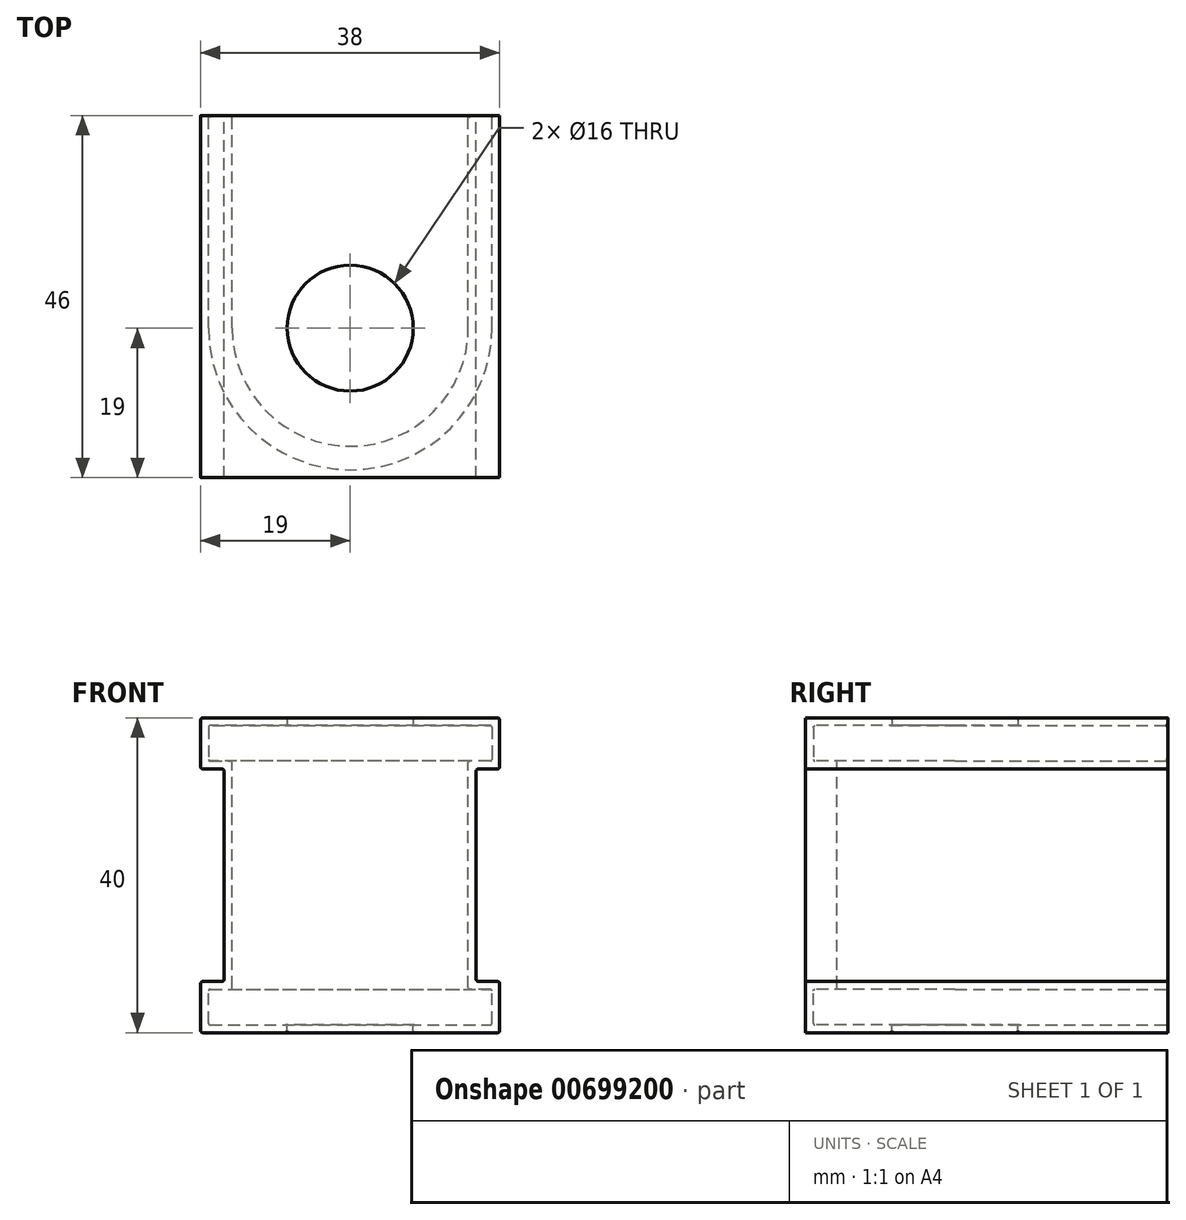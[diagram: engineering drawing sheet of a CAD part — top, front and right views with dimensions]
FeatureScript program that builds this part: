
annotation { "Feature Type Name" : "Feature", "Feature Type Description" : "" }
export const myFeature = defineFeature(function(context is Context, id is Id, definition is map)
    precondition{}
    {
        {
            var Q0;
            Q0=qCreatedBy(makeId("Top.planeOp"),FACE);
            var sketch = newSketch(context, id + "F0", { "sketchPlane" : qUnion([Q0])});
            skCircle(sketch, "E0", {"center": v(0, 0) * mm, "radius": 8 * mm});
            skArc(sketch, "E1", {"start": v(-15, 0) * mm, "mid": v(0, -15) * mm, "end": v(15, 0) * mm});
            skArc(sketch, "E2", {"start": v(-18, 0) * mm, "mid": v(0, -18) * mm, "end": v(18, 0) * mm});
            skLineSegment(sketch, "E3", {"start": v(-18, 0) * mm, "end": v(-18, 17) * mm});
            skLineSegment(sketch, "E4", {"start": v(-18, 17) * mm, "end": v(0, 17) * mm});
            skLineSegment(sketch, "E5", {"start": v(18, 0) * mm, "end": v(18, 17) * mm});
            skLineSegment(sketch, "E6", {"start": v(18, 17) * mm, "end": v(0, 17) * mm});
            skLineSegment(sketch, "E7", {"start": v(-15, 0) * mm, "end": v(-15, 17) * mm});
            skLineSegment(sketch, "E8", {"start": v(15, 0) * mm, "end": v(15, 17) * mm});
            skLineSegment(sketch, "E9.0", {"start": v(-19, 18) * mm, "end": v(0, 18) * mm});
            skLineSegment(sketch, "E9.1", {"start": v(-19, 0) * mm, "end": v(-19, 18) * mm});
            skLineSegment(sketch, "E9.2", {"start": v(19, 18) * mm, "end": v(0, 18) * mm});
            skLineSegment(sketch, "E9.3", {"start": v(19, 0) * mm, "end": v(19, 18) * mm});
            skArc(sketch, "E9.4", {"start": v(-19, 0) * mm, "mid": v(0, -19) * mm, "end": v(19, 0) * mm});
            skLineSegment(sketch, "E10", {"start": v(-19, 0) * mm, "end": v(-19, -19) * mm});
            skPoint(sketch, "E10.endSnap0", {"position": v(0, -19) * mm});
            skLineSegment(sketch, "E11", {"start": v(-19, -19) * mm, "end": v(0, -19) * mm});
            skLineSegment(sketch, "E12", {"start": v(19, 0) * mm, "end": v(19, -19) * mm});
            skLineSegment(sketch, "E13", {"start": v(19, -19) * mm, "end": v(0, -19) * mm});
            skSolve(sketch);
        }
        {
            var Q0;
            Q0=makeQuery(id+"F0.imprint","IMPRINT",FACE,{"disambiguationData":[TD([[makeQuery(id+"F0.imprint","IMPRINT",EDGE,{"derivedFrom":sQuery(id+"F0.wireOp",EDGE,"E2")}),-1.0]])]});
            extrude(context, id + "F1", {"entities" : qUnion([Q0]), "oppositeDirection" : true, "depth" : (38 / 2 + 1) * mm, "offsetDistance" : 25 * mm});
        }
        {
            var Q0;
            Q0=makeQuery(id+"F0.imprint","IMPRINT",FACE,{"disambiguationData":[TD([[makeQuery(id+"F0.imprint","IMPRINT",EDGE,{"derivedFrom":sQuery(id+"F0.wireOp",EDGE,"E0")}),-1.0]])]});
            extrude(context, id + "F2", {"entities" : qUnion([Q0]), "operationType" : NewBodyOperationType.ADD, "oppositeDirection" : true, "depth" : (38 / 2 + 1) * mm, "offsetDistance" : 25 * mm, "hasSecondDirection" : true, "secondDirectionOppositeDirection" : true, "secondDirectionDepth" : (38 / 2) * mm});
        }
        {
            var Q0;
            {var subQ0=makeQuery(id+"F1.opExtrude","SWEPT_FACE",FACE,{"disambiguationData":[OSD([sQuery(id+"F0.wireOp",EDGE,"E9.0"),sQuery(id+"F0.wireOp",EDGE,"E9.2")])]});Q0=makeQuery(id+"FkgVPa9aZE5Qvnv_1.boolean.opBoolean","MERGE",FACE,{"derivedFrom":[subQ0,makeQuery(id+"FkgVPa9aZE5Qvnv_1.opPattern","COPY",FACE,{"derivedFrom":subQ0,"instanceName":"1"})]});}
            extrude(context, id + "F3", {"entities" : qUnion([Q0]), "operationType" : NewBodyOperationType.REMOVE, "oppositeDirection" : true, "depth" : 1 * mm, "offsetDistance" : 25 * mm});
        }
        {
            var Q0;
            Q0=makeQuery(id+"F0.imprint","IMPRINT",FACE,{"disambiguationData":[TD([[makeQuery(id+"F0.imprint","IMPRINT",EDGE,{"derivedFrom":sQuery(id+"F0.wireOp",EDGE,"E1")}),-1.0]])]});
            extrude(context, id + "F4", {"entities" : qUnion([Q0]), "operationType" : NewBodyOperationType.ADD, "oppositeDirection" : true, "depth" : 20 * mm, "offsetDistance" : 25 * mm, "hasSecondDirection" : true, "secondDirectionOppositeDirection" : true, "secondDirectionDepth" : 19 * mm});
        }
        {
            var Q0;
            Q0=makeQuery(id+"F0.imprint","IMPRINT",FACE,{"disambiguationData":[TD([[makeQuery(id+"F0.imprint","IMPRINT",EDGE,{"derivedFrom":sQuery(id+"F0.wireOp",EDGE,"E1")}),-1.0]])]});
            extrude(context, id + "F5", {"entities" : qUnion([Q0]), "operationType" : NewBodyOperationType.ADD, "oppositeDirection" : true, "depth" : (29 / 2) * mm, "offsetDistance" : 25 * mm});
        }
        {
            var Q0;
            {var subQ0=sQuery(id+"F0.wireOp",EDGE,"E10");Q0=makeQuery(id+"F0.imprint","IMPRINT",FACE,{"disambiguationData":[TD([[makeQuery(id+"F0.imprint","IMPRINT",EDGE,{"derivedFrom":subQ0}),1.0]])]});}
            var Q1;
            {var subQ0=sQuery(id+"F0.wireOp",EDGE,"E12");Q1=makeQuery(id+"F0.imprint","IMPRINT",FACE,{"disambiguationData":[TD([[makeQuery(id+"F0.imprint","IMPRINT",EDGE,{"derivedFrom":subQ0}),-1.0]])]});}
            extrude(context, id + "F6", {"entities" : qUnion([Q0, Q1]), "operationType" : NewBodyOperationType.ADD, "oppositeDirection" : true, "depth" : 20 * mm, "offsetDistance" : 25 * mm});
        }
        {
            var Q0;
            Q0=makeQuery(id+"F3.boolean.opBoolean","SPLIT",BODY,{"disambiguationData":[OD(0.0)],"derivedFrom":makeQuery(id+"F1.opExtrude","SWEPT_BODY",BODY,{"disambiguationData":[OSD([sQuery(id+"F0.wireOp",EDGE,"E2"),sQuery(id+"F0.wireOp",EDGE,"E3"),sQuery(id+"F0.wireOp",EDGE,"E4"),sQuery(id+"F0.wireOp",EDGE,"E5"),sQuery(id+"F0.wireOp",EDGE,"E6"),sQuery(id+"F0.wireOp",EDGE,"E9.0"),sQuery(id+"F0.wireOp",EDGE,"E9.1"),sQuery(id+"F0.wireOp",EDGE,"E9.2"),sQuery(id+"F0.wireOp",EDGE,"E9.3"),sQuery(id+"F0.wireOp",EDGE,"E9.4")])]})});
            var Q1;
            Q1=qCreatedBy(makeId("Top.planeOp"),FACE);
            mirror(context, id + "F7", {"operationType" : NewBodyOperationType.ADD, "entities" : qUnion([Q0]), "mirrorPlane" : qUnion([Q1])});
        }
        {
            var Q0;
            {var subQ0=sQuery(id+"F0.wireOp",EDGE,"E6");var subQ1=sQuery(id+"F0.wireOp",EDGE,"E4");var subQ3=sQuery(id+"F0.wireOp",EDGE,"E5");var subQ5=sQuery(id+"F0.wireOp",EDGE,"E9.2");var subQ7=sQuery(id+"F0.wireOp",EDGE,"E9.0");var subQ8=sQuery(id+"F0.wireOp",EDGE,"E3");var subQ13=sQuery(id+"F0.wireOp",EDGE,"E7");var subQ17=makeQuery(id+"F3.opExtrude","CAP_FACE",FACE,{"disambiguationData":[OSD([subQ7,subQ5])],"isStart":false});var subQ18=makeQuery(id+"F5.boolean.opBoolean","MERGE",FACE,{"derivedFrom":[makeQuery(id+"F4.boolean.opBoolean","MERGE",FACE,{"derivedFrom":[makeQuery(id+"F3.boolean.opBoolean","COPY",FACE,{"disambiguationData":[TD([makeQuery(id+"F2.opExtrude","SWEPT_FACE",FACE,{"disambiguationData":[OSD([subQ13])]})])],"derivedFrom":subQ17}),makeQuery(id+"F3.boolean.opBoolean","COPY",FACE,{"disambiguationData":[TD([makeQuery(id+"F1.opExtrude","SWEPT_FACE",FACE,{"disambiguationData":[OSD([subQ8])]})])],"derivedFrom":subQ17}),makeQuery(id+"F3.boolean.opBoolean","COPY",FACE,{"disambiguationData":[TD([makeQuery(id+"F1.opExtrude","SWEPT_FACE",FACE,{"disambiguationData":[OSD([subQ3])]})])],"derivedFrom":subQ17}),makeQuery(id+"F4.opExtrude","SWEPT_FACE",FACE,{"disambiguationData":[OSD([subQ1])]}),makeQuery(id+"F4.opExtrude","SWEPT_FACE",FACE,{"disambiguationData":[OSD([subQ0])]})]}),makeQuery(id+"F5.opExtrude","SWEPT_FACE",FACE,{"disambiguationData":[OSD([subQ1])]}),makeQuery(id+"F5.opExtrude","SWEPT_FACE",FACE,{"disambiguationData":[OSD([subQ0])]})]});Q0=makeQuery(id+"F7.boolean.opBoolean","MERGE",FACE,{"derivedFrom":[subQ18,makeQuery(id+"F7.opPattern","COPY",FACE,{"derivedFrom":subQ18,"instanceName":"1"})]});}
            var sketch = newSketch(context, id + "F8", { "sketchPlane" : qUnion([Q0])});
            skLineSegment(sketch, "E14", {"start": v(-19, 13.5) * mm, "end": v(-16, 13.5) * mm});
            skLineSegment(sketch, "E15", {"start": v(-16, 13.5) * mm, "end": v(-16, -13.5) * mm});
            skLineSegment(sketch, "E16", {"start": v(-16, -13.5) * mm, "end": v(-19, -13.5) * mm});
            skLineSegment(sketch, "E17", {"start": v(-19, -13.5) * mm, "end": v(-19, 13.5) * mm});
            skLineSegment(sketch, "E18.MirrorCS", {"start": v(-13, 13.5) * mm, "end": v(-16, 13.5) * mm});
            skLineSegment(sketch, "E19.MirrorCS", {"start": v(16, 13.5) * mm, "end": v(16, -13.5) * mm});
            skLineSegment(sketch, "E20.MirrorCS", {"start": v(19, 13.5) * mm, "end": v(16, 13.5) * mm});
            skLineSegment(sketch, "E21.MirrorCS", {"start": v(19, -13.5) * mm, "end": v(19, 13.5) * mm});
            skLineSegment(sketch, "E22.MirrorCS", {"start": v(16, -13.5) * mm, "end": v(19, -13.5) * mm});
            skSolve(sketch);
        }
        {
            var Q0;
            Q0 = qSketchRegion(id + "F8", true);
            extrude(context, id + "F9", {"entities" : qUnion([Q0]), "operationType" : NewBodyOperationType.REMOVE, "oppositeDirection" : true, "depth" : 38.8 * mm, "offsetDistance" : 25 * mm});
        }
        {
            var Q0;
            {var subQ0=sQuery(id+"F0.wireOp",EDGE,"E6");var subQ1=sQuery(id+"F0.wireOp",EDGE,"E4");var subQ3=sQuery(id+"F0.wireOp",EDGE,"E5");var subQ5=sQuery(id+"F0.wireOp",EDGE,"E9.2");var subQ7=sQuery(id+"F0.wireOp",EDGE,"E9.0");var subQ8=sQuery(id+"F0.wireOp",EDGE,"E3");var subQ13=sQuery(id+"F0.wireOp",EDGE,"E7");var subQ17=makeQuery(id+"F3.opExtrude","CAP_FACE",FACE,{"disambiguationData":[OSD([subQ7,subQ5])],"isStart":false});var subQ18=makeQuery(id+"F5.boolean.opBoolean","MERGE",FACE,{"derivedFrom":[makeQuery(id+"F4.boolean.opBoolean","MERGE",FACE,{"derivedFrom":[makeQuery(id+"F3.boolean.opBoolean","COPY",FACE,{"disambiguationData":[TD([makeQuery(id+"F2.opExtrude","SWEPT_FACE",FACE,{"disambiguationData":[OSD([subQ13])]})])],"derivedFrom":subQ17}),makeQuery(id+"F3.boolean.opBoolean","COPY",FACE,{"disambiguationData":[TD([makeQuery(id+"F1.opExtrude","SWEPT_FACE",FACE,{"disambiguationData":[OSD([subQ8])]})])],"derivedFrom":subQ17}),makeQuery(id+"F3.boolean.opBoolean","COPY",FACE,{"disambiguationData":[TD([makeQuery(id+"F1.opExtrude","SWEPT_FACE",FACE,{"disambiguationData":[OSD([subQ3])]})])],"derivedFrom":subQ17}),makeQuery(id+"F4.opExtrude","SWEPT_FACE",FACE,{"disambiguationData":[OSD([subQ1])]}),makeQuery(id+"F4.opExtrude","SWEPT_FACE",FACE,{"disambiguationData":[OSD([subQ0])]})]}),makeQuery(id+"F5.opExtrude","SWEPT_FACE",FACE,{"disambiguationData":[OSD([subQ1])]}),makeQuery(id+"F5.opExtrude","SWEPT_FACE",FACE,{"disambiguationData":[OSD([subQ0])]})]});Q0=makeQuery(id+"F7.boolean.opBoolean","MERGE",FACE,{"derivedFrom":[subQ18,makeQuery(id+"F7.opPattern","COPY",FACE,{"derivedFrom":subQ18,"instanceName":"1"})]});}
            extrude(context, id + "F10", {"entities" : qUnion([Q0]), "operationType" : NewBodyOperationType.ADD, "depth" : 10 * mm, "offsetDistance" : 25 * mm});
        }
        {
            var Q0;
            {var subQ0=sQuery(id+"F0.wireOp",EDGE,"E7");var subQ1=sQuery(id+"F0.wireOp",EDGE,"E4");Q0=makeQuery(id+"F10.boolean.opBoolean","MERGE",EDGE,{"derivedFrom":[makeQuery(id+"F7.opPattern","COPY",EDGE,{"derivedFrom":makeQuery(id+"F5.opExtrude","CAP_EDGE",EDGE,{"disambiguationData":[OSD([subQ0])],"isStart":false}),"instanceName":"1"}),makeQuery(id+"F10.opExtrude","SWEPT_EDGE",EDGE,{"disambiguationData":[OSD([subQ1,subQ0]),TDD([makeQuery(id+"F7.opPattern","COPY",VERTEX,{"derivedFrom":makeQuery(id+"F5.opExtrude","CAP_VERTEX",VERTEX,{"disambiguationData":[OSD([subQ1,subQ0])],"isStart":false}),"instanceName":"1"})])]})]});}
            var Q1;
            Q1=makeQuery(id+"F7.opPattern","COPY",EDGE,{"derivedFrom":makeQuery(id+"F5.opExtrude","CAP_EDGE",EDGE,{"disambiguationData":[OSD([sQuery(id+"F0.wireOp",EDGE,"E1")])],"isStart":false}),"instanceName":"1"});
            var Q2;
            {var subQ0=sQuery(id+"F0.wireOp",EDGE,"E7");var subQ1=sQuery(id+"F0.wireOp",EDGE,"E4");Q2=makeQuery(id+"F10.boolean.opBoolean","MERGE",EDGE,{"derivedFrom":[makeQuery(id+"F5.opExtrude","CAP_EDGE",EDGE,{"disambiguationData":[OSD([subQ0])],"isStart":false}),makeQuery(id+"F10.opExtrude","SWEPT_EDGE",EDGE,{"disambiguationData":[OSD([subQ1,subQ0]),TDD([makeQuery(id+"F5.opExtrude","CAP_VERTEX",VERTEX,{"disambiguationData":[OSD([subQ1,subQ0])],"isStart":false})])]})]});}
            var Q3;
            Q3=makeQuery(id+"F5.opExtrude","CAP_EDGE",EDGE,{"disambiguationData":[OSD([sQuery(id+"F0.wireOp",EDGE,"E1")])],"isStart":false});
            var Q4;
            {var subQ0=sQuery(id+"F0.wireOp",EDGE,"E4");var subQ1=sQuery(id+"F0.wireOp",EDGE,"E3");Q4=makeQuery(id+"F10.boolean.opBoolean","MERGE",EDGE,{"derivedFrom":[makeQuery(id+"F7.opPattern","COPY",EDGE,{"derivedFrom":makeQuery(id+"F5.opExtrude","CAP_EDGE",EDGE,{"disambiguationData":[OSD([subQ1])],"isStart":false}),"instanceName":"1"}),makeQuery(id+"F10.opExtrude","SWEPT_EDGE",EDGE,{"disambiguationData":[OSD([subQ1,subQ0]),TDD([makeQuery(id+"F7.opPattern","COPY",VERTEX,{"derivedFrom":makeQuery(id+"F5.opExtrude","CAP_VERTEX",VERTEX,{"disambiguationData":[OSD([subQ1,subQ0])],"isStart":false}),"instanceName":"1"})])]})]});}
            var Q5;
            {var subQ0=sQuery(id+"F0.wireOp",EDGE,"E6");var subQ1=sQuery(id+"F0.wireOp",EDGE,"E4");Q5=makeQuery(id+"F10.boolean.opBoolean","MERGE",FACE,{"derivedFrom":[makeQuery(id+"F7.opPattern","COPY",FACE,{"derivedFrom":makeQuery(id+"F5.opExtrude","CAP_FACE",FACE,{"disambiguationData":[OSD([sQuery(id+"F0.wireOp",EDGE,"E1"),sQuery(id+"F0.wireOp",EDGE,"E2"),sQuery(id+"F0.wireOp",EDGE,"E3"),subQ1,sQuery(id+"F0.wireOp",EDGE,"E5"),subQ0,sQuery(id+"F0.wireOp",EDGE,"E7"),sQuery(id+"F0.wireOp",EDGE,"E8")])],"isStart":false}),"instanceName":"1"}),makeQuery(id+"F10.opExtrude","SWEPT_FACE",FACE,{"disambiguationData":[OSD([subQ1]),TDD([makeQuery(id+"F7.opPattern","COPY",EDGE,{"derivedFrom":makeQuery(id+"F5.opExtrude","CAP_EDGE",EDGE,{"disambiguationData":[OSD([subQ1])],"isStart":false}),"instanceName":"1"})])]}),makeQuery(id+"F10.opExtrude","SWEPT_FACE",FACE,{"disambiguationData":[OSD([subQ0]),TDD([makeQuery(id+"F7.opPattern","COPY",EDGE,{"derivedFrom":makeQuery(id+"F5.opExtrude","CAP_EDGE",EDGE,{"disambiguationData":[OSD([subQ0])],"isStart":false}),"instanceName":"1"})])]})]});}
            var Q6;
            Q6=makeQuery(id+"F4.opExtrude","CAP_EDGE",EDGE,{"disambiguationData":[OSD([sQuery(id+"F0.wireOp",EDGE,"E2")])],"isStart":true});
            var Q7;
            {var subQ0=sQuery(id+"F0.wireOp",EDGE,"E4");var subQ1=sQuery(id+"F0.wireOp",EDGE,"E3");Q7=makeQuery(id+"F10.boolean.opBoolean","MERGE",EDGE,{"derivedFrom":[makeQuery(id+"F4.opExtrude","CAP_EDGE",EDGE,{"disambiguationData":[OSD([subQ1])],"isStart":true}),makeQuery(id+"F10.opExtrude","SWEPT_EDGE",EDGE,{"disambiguationData":[OSD([subQ1,subQ0]),TDD([makeQuery(id+"F4.opExtrude","CAP_VERTEX",VERTEX,{"disambiguationData":[OSD([subQ1,subQ0])],"isStart":true})])]})]});}
            var Q8;
            {var subQ0=sQuery(id+"F0.wireOp",EDGE,"E6");var subQ1=sQuery(id+"F0.wireOp",EDGE,"E5");Q8=makeQuery(id+"F10.boolean.opBoolean","MERGE",EDGE,{"derivedFrom":[makeQuery(id+"F4.opExtrude","CAP_EDGE",EDGE,{"disambiguationData":[OSD([subQ1])],"isStart":true}),makeQuery(id+"F10.opExtrude","SWEPT_EDGE",EDGE,{"disambiguationData":[OSD([subQ1,subQ0]),TDD([makeQuery(id+"F4.opExtrude","CAP_VERTEX",VERTEX,{"disambiguationData":[OSD([subQ1,subQ0])],"isStart":true})])]})]});}
            var Q9;
            {var subQ0=sQuery(id+"F0.wireOp",EDGE,"E8");var subQ1=sQuery(id+"F0.wireOp",EDGE,"E6");Q9=makeQuery(id+"F10.boolean.opBoolean","MERGE",EDGE,{"derivedFrom":[makeQuery(id+"F5.opExtrude","CAP_EDGE",EDGE,{"disambiguationData":[OSD([subQ0])],"isStart":false}),makeQuery(id+"F10.opExtrude","SWEPT_EDGE",EDGE,{"disambiguationData":[OSD([subQ1,subQ0]),TDD([makeQuery(id+"F5.opExtrude","CAP_VERTEX",VERTEX,{"disambiguationData":[OSD([subQ1,subQ0])],"isStart":false})])]})]});}
            var Q10;
            Q10=makeQuery(id+"F5.opExtrude","CAP_EDGE",EDGE,{"disambiguationData":[OSD([sQuery(id+"F0.wireOp",EDGE,"E2")])],"isStart":false});
            var Q11;
            {var subQ0=sQuery(id+"F0.wireOp",EDGE,"E4");var subQ1=sQuery(id+"F0.wireOp",EDGE,"E3");Q11=makeQuery(id+"F10.boolean.opBoolean","MERGE",EDGE,{"derivedFrom":[makeQuery(id+"F5.opExtrude","CAP_EDGE",EDGE,{"disambiguationData":[OSD([subQ1])],"isStart":false}),makeQuery(id+"F10.opExtrude","SWEPT_EDGE",EDGE,{"disambiguationData":[OSD([subQ1,subQ0]),TDD([makeQuery(id+"F5.opExtrude","CAP_VERTEX",VERTEX,{"disambiguationData":[OSD([subQ1,subQ0])],"isStart":false})])]})]});}
            var Q12;
            {var subQ0=sQuery(id+"F0.wireOp",EDGE,"E6");var subQ1=sQuery(id+"F0.wireOp",EDGE,"E5");Q12=makeQuery(id+"F10.boolean.opBoolean","MERGE",EDGE,{"derivedFrom":[makeQuery(id+"F5.opExtrude","CAP_EDGE",EDGE,{"disambiguationData":[OSD([subQ1])],"isStart":false}),makeQuery(id+"F10.opExtrude","SWEPT_EDGE",EDGE,{"disambiguationData":[OSD([subQ1,subQ0]),TDD([makeQuery(id+"F5.opExtrude","CAP_VERTEX",VERTEX,{"disambiguationData":[OSD([subQ1,subQ0])],"isStart":false})])]})]});}
            var Q13;
            {var subQ0=sQuery(id+"F0.wireOp",EDGE,"E6");var subQ1=sQuery(id+"F0.wireOp",EDGE,"E5");Q13=makeQuery(id+"F10.boolean.opBoolean","MERGE",EDGE,{"derivedFrom":[makeQuery(id+"F7.opPattern","COPY",EDGE,{"derivedFrom":makeQuery(id+"F4.opExtrude","CAP_EDGE",EDGE,{"disambiguationData":[OSD([subQ1])],"isStart":true}),"instanceName":"1"}),makeQuery(id+"F10.opExtrude","SWEPT_EDGE",EDGE,{"disambiguationData":[OSD([subQ1,subQ0]),TDD([makeQuery(id+"F7.opPattern","COPY",VERTEX,{"derivedFrom":makeQuery(id+"F4.opExtrude","CAP_VERTEX",VERTEX,{"disambiguationData":[OSD([subQ1,subQ0])],"isStart":true}),"instanceName":"1"})])]})]});}
            var Q14;
            Q14=makeQuery(id+"F7.opPattern","COPY",EDGE,{"derivedFrom":makeQuery(id+"F4.opExtrude","CAP_EDGE",EDGE,{"disambiguationData":[OSD([sQuery(id+"F0.wireOp",EDGE,"E2")])],"isStart":true}),"instanceName":"1"});
            var Q15;
            {var subQ0=sQuery(id+"F0.wireOp",EDGE,"E4");var subQ1=sQuery(id+"F0.wireOp",EDGE,"E3");Q15=makeQuery(id+"F10.boolean.opBoolean","MERGE",EDGE,{"derivedFrom":[makeQuery(id+"F7.opPattern","COPY",EDGE,{"derivedFrom":makeQuery(id+"F4.opExtrude","CAP_EDGE",EDGE,{"disambiguationData":[OSD([subQ1])],"isStart":true}),"instanceName":"1"}),makeQuery(id+"F10.opExtrude","SWEPT_EDGE",EDGE,{"disambiguationData":[OSD([subQ1,subQ0]),TDD([makeQuery(id+"F7.opPattern","COPY",VERTEX,{"derivedFrom":makeQuery(id+"F4.opExtrude","CAP_VERTEX",VERTEX,{"disambiguationData":[OSD([subQ1,subQ0])],"isStart":true}),"instanceName":"1"})])]})]});}
            var Q16;
            {var subQ0=sQuery(id+"F0.wireOp",EDGE,"E4");var subQ1=sQuery(id+"F0.wireOp",EDGE,"E3");Q16=makeQuery(id+"F10.opExtrude","CAP_EDGE",EDGE,{"disambiguationData":[OSD([subQ1,subQ0]),TDD([makeQuery(id+"F7.opPattern","COPY",EDGE,{"derivedFrom":makeQuery(id+"F1.opExtrude","SWEPT_EDGE",EDGE,{"disambiguationData":[OSD([subQ1,subQ0])]}),"instanceName":"1"})])],"isStart":false});}
            fillet(context, id + "F11", {"entities" : qUnion([Q0, Q1, Q2, Q3, Q4, Q5, Q6, Q7, Q8, Q9, Q10, Q11, Q12, Q13, Q14, Q15, Q16]), "radius" : 0.2 * mm, "tangentPropagation" : true, "allowEdgeOverflow" : false});
        }
        {
            var Q0;
            {var subQ0=sQuery(id+"F0.wireOp",EDGE,"E9.3");var subQ1=sQuery(id+"F0.wireOp",EDGE,"E9.2");Q0=makeQuery(id+"F10.boolean.opBoolean","MERGE",EDGE,{"derivedFrom":[makeQuery(id+"F7.opPattern","COPY",EDGE,{"derivedFrom":makeQuery(id+"F6.boolean.opBoolean","MERGE",EDGE,{"derivedFrom":[makeQuery(id+"F1.opExtrude","CAP_EDGE",EDGE,{"disambiguationData":[OSD([subQ0])],"isStart":false}),makeQuery(id+"F6.opExtrude","CAP_EDGE",EDGE,{"disambiguationData":[OSD([sQuery(id+"F0.wireOp",EDGE,"E12")])],"isStart":false})]}),"instanceName":"1"}),makeQuery(id+"F10.opExtrude","SWEPT_EDGE",EDGE,{"disambiguationData":[OSD([subQ1,subQ0]),TDD([makeQuery(id+"F7.opPattern","COPY",VERTEX,{"derivedFrom":makeQuery(id+"F3.boolean.opBoolean","COPY",VERTEX,{"derivedFrom":makeQuery(id+"F3.opExtrude","CAP_VERTEX",VERTEX,{"disambiguationData":[OSD([subQ1,subQ0]),TDD([makeQuery(id+"F1.opExtrude","CAP_VERTEX",VERTEX,{"disambiguationData":[OSD([subQ1,subQ0])],"isStart":false})])],"isStart":false})}),"instanceName":"1"})])]})]});}
            var Q1;
            {var subQ0=sQuery(id+"F8.wireOp",EDGE,"E17");var subQ1=sQuery(id+"F8.wireOp",EDGE,"E14");var subQ2=sQuery(id+"F0.wireOp",EDGE,"E9.3");var subQ3=sQuery(id+"F0.wireOp",EDGE,"E9.2");Q1=makeQuery(id+"F10.boolean.opBoolean","MERGE",EDGE,{"derivedFrom":[makeQuery(id+"F9.boolean.opBoolean","COPY",EDGE,{"derivedFrom":makeQuery(id+"F9.opExtrude","SWEPT_EDGE",EDGE,{"disambiguationData":[OSD([subQ3,subQ2,subQ1,subQ0])]})}),makeQuery(id+"F10.opExtrude","SWEPT_EDGE",EDGE,{"disambiguationData":[OSD([subQ3,subQ2,subQ1,subQ0])]})]});}
            var Q2;
            {var subQ0=sQuery(id+"F8.wireOp",EDGE,"E15");var subQ1=sQuery(id+"F8.wireOp",EDGE,"E14");Q2=makeQuery(id+"F10.boolean.opBoolean","MERGE",EDGE,{"derivedFrom":[makeQuery(id+"F9.boolean.opBoolean","COPY",EDGE,{"derivedFrom":makeQuery(id+"F9.opExtrude","SWEPT_EDGE",EDGE,{"disambiguationData":[OSD([subQ1,subQ0])]})}),makeQuery(id+"F10.opExtrude","SWEPT_EDGE",EDGE,{"disambiguationData":[OSD([subQ1,subQ0])]})]});}
            var Q3;
            {var subQ0=sQuery(id+"F8.wireOp",EDGE,"E16");var subQ1=sQuery(id+"F8.wireOp",EDGE,"E15");Q3=makeQuery(id+"F10.boolean.opBoolean","MERGE",EDGE,{"derivedFrom":[makeQuery(id+"F9.boolean.opBoolean","COPY",EDGE,{"derivedFrom":makeQuery(id+"F9.opExtrude","SWEPT_EDGE",EDGE,{"disambiguationData":[OSD([subQ1,subQ0])]})}),makeQuery(id+"F10.opExtrude","SWEPT_EDGE",EDGE,{"disambiguationData":[OSD([subQ1,subQ0])]})]});}
            var Q4;
            {var subQ0=sQuery(id+"F8.wireOp",EDGE,"E17");var subQ1=sQuery(id+"F8.wireOp",EDGE,"E16");var subQ2=sQuery(id+"F0.wireOp",EDGE,"E9.3");var subQ3=sQuery(id+"F0.wireOp",EDGE,"E9.2");Q4=makeQuery(id+"F10.boolean.opBoolean","MERGE",EDGE,{"derivedFrom":[makeQuery(id+"F9.boolean.opBoolean","COPY",EDGE,{"derivedFrom":makeQuery(id+"F9.opExtrude","SWEPT_EDGE",EDGE,{"disambiguationData":[OSD([subQ3,subQ2,subQ1,subQ0])]})}),makeQuery(id+"F10.opExtrude","SWEPT_EDGE",EDGE,{"disambiguationData":[OSD([subQ3,subQ2,subQ1,subQ0])]})]});}
            var Q5;
            {var subQ0=sQuery(id+"F0.wireOp",EDGE,"E9.3");var subQ1=sQuery(id+"F0.wireOp",EDGE,"E9.2");Q5=makeQuery(id+"F10.boolean.opBoolean","MERGE",EDGE,{"derivedFrom":[makeQuery(id+"F6.boolean.opBoolean","MERGE",EDGE,{"derivedFrom":[makeQuery(id+"F1.opExtrude","CAP_EDGE",EDGE,{"disambiguationData":[OSD([subQ0])],"isStart":false}),makeQuery(id+"F6.opExtrude","CAP_EDGE",EDGE,{"disambiguationData":[OSD([sQuery(id+"F0.wireOp",EDGE,"E12")])],"isStart":false})]}),makeQuery(id+"F10.opExtrude","SWEPT_EDGE",EDGE,{"disambiguationData":[OSD([subQ1,subQ0]),TDD([makeQuery(id+"F3.boolean.opBoolean","COPY",VERTEX,{"derivedFrom":makeQuery(id+"F3.opExtrude","CAP_VERTEX",VERTEX,{"disambiguationData":[OSD([subQ1,subQ0]),TDD([makeQuery(id+"F1.opExtrude","CAP_VERTEX",VERTEX,{"disambiguationData":[OSD([subQ1,subQ0])],"isStart":false})])],"isStart":false})})])]})]});}
            var Q6;
            {var subQ0=sQuery(id+"F0.wireOp",EDGE,"E9.1");var subQ1=sQuery(id+"F0.wireOp",EDGE,"E9.0");Q6=makeQuery(id+"F10.boolean.opBoolean","MERGE",EDGE,{"derivedFrom":[makeQuery(id+"F6.boolean.opBoolean","MERGE",EDGE,{"derivedFrom":[makeQuery(id+"F1.opExtrude","CAP_EDGE",EDGE,{"disambiguationData":[OSD([subQ0])],"isStart":false}),makeQuery(id+"F6.opExtrude","CAP_EDGE",EDGE,{"disambiguationData":[OSD([sQuery(id+"F0.wireOp",EDGE,"E10")])],"isStart":false})]}),makeQuery(id+"F10.opExtrude","SWEPT_EDGE",EDGE,{"disambiguationData":[OSD([subQ1,subQ0]),TDD([makeQuery(id+"F3.boolean.opBoolean","COPY",VERTEX,{"derivedFrom":makeQuery(id+"F3.opExtrude","CAP_VERTEX",VERTEX,{"disambiguationData":[OSD([subQ1,subQ0]),TDD([makeQuery(id+"F1.opExtrude","CAP_VERTEX",VERTEX,{"disambiguationData":[OSD([subQ1,subQ0])],"isStart":false})])],"isStart":false})})])]})]});}
            var Q7;
            {var subQ0=sQuery(id+"F8.wireOp",EDGE,"E22.MirrorCS");var subQ1=sQuery(id+"F8.wireOp",EDGE,"E21.MirrorCS");var subQ2=sQuery(id+"F0.wireOp",EDGE,"E9.1");var subQ3=sQuery(id+"F0.wireOp",EDGE,"E9.0");Q7=makeQuery(id+"F10.boolean.opBoolean","MERGE",EDGE,{"derivedFrom":[makeQuery(id+"F9.boolean.opBoolean","COPY",EDGE,{"derivedFrom":makeQuery(id+"F9.opExtrude","SWEPT_EDGE",EDGE,{"disambiguationData":[OSD([subQ3,subQ2,subQ1,subQ0])]})}),makeQuery(id+"F10.opExtrude","SWEPT_EDGE",EDGE,{"disambiguationData":[OSD([subQ3,subQ2,subQ1,subQ0])]})]});}
            var Q8;
            {var subQ0=sQuery(id+"F8.wireOp",EDGE,"E22.MirrorCS");var subQ1=sQuery(id+"F8.wireOp",EDGE,"E19.MirrorCS");Q8=makeQuery(id+"F10.boolean.opBoolean","MERGE",EDGE,{"derivedFrom":[makeQuery(id+"F9.boolean.opBoolean","COPY",EDGE,{"derivedFrom":makeQuery(id+"F9.opExtrude","SWEPT_EDGE",EDGE,{"disambiguationData":[OSD([subQ1,subQ0])]})}),makeQuery(id+"F10.opExtrude","SWEPT_EDGE",EDGE,{"disambiguationData":[OSD([subQ1,subQ0])]})]});}
            var Q9;
            {var subQ0=sQuery(id+"F0.wireOp",EDGE,"E9.1");var subQ1=sQuery(id+"F0.wireOp",EDGE,"E9.0");Q9=makeQuery(id+"F10.boolean.opBoolean","MERGE",EDGE,{"derivedFrom":[makeQuery(id+"F7.opPattern","COPY",EDGE,{"derivedFrom":makeQuery(id+"F6.boolean.opBoolean","MERGE",EDGE,{"derivedFrom":[makeQuery(id+"F1.opExtrude","CAP_EDGE",EDGE,{"disambiguationData":[OSD([subQ0])],"isStart":false}),makeQuery(id+"F6.opExtrude","CAP_EDGE",EDGE,{"disambiguationData":[OSD([sQuery(id+"F0.wireOp",EDGE,"E10")])],"isStart":false})]}),"instanceName":"1"}),makeQuery(id+"F10.opExtrude","SWEPT_EDGE",EDGE,{"disambiguationData":[OSD([subQ1,subQ0]),TDD([makeQuery(id+"F7.opPattern","COPY",VERTEX,{"derivedFrom":makeQuery(id+"F3.boolean.opBoolean","COPY",VERTEX,{"derivedFrom":makeQuery(id+"F3.opExtrude","CAP_VERTEX",VERTEX,{"disambiguationData":[OSD([subQ1,subQ0]),TDD([makeQuery(id+"F1.opExtrude","CAP_VERTEX",VERTEX,{"disambiguationData":[OSD([subQ1,subQ0])],"isStart":false})])],"isStart":false})}),"instanceName":"1"})])]})]});}
            var Q10;
            {var subQ0=sQuery(id+"F8.wireOp",EDGE,"E21.MirrorCS");var subQ1=sQuery(id+"F8.wireOp",EDGE,"E20.MirrorCS");var subQ2=sQuery(id+"F0.wireOp",EDGE,"E9.1");var subQ3=sQuery(id+"F0.wireOp",EDGE,"E9.0");Q10=makeQuery(id+"F10.boolean.opBoolean","MERGE",EDGE,{"derivedFrom":[makeQuery(id+"F9.boolean.opBoolean","COPY",EDGE,{"derivedFrom":makeQuery(id+"F9.opExtrude","SWEPT_EDGE",EDGE,{"disambiguationData":[OSD([subQ3,subQ2,subQ1,subQ0])]})}),makeQuery(id+"F10.opExtrude","SWEPT_EDGE",EDGE,{"disambiguationData":[OSD([subQ3,subQ2,subQ1,subQ0])]})]});}
            var Q11;
            {var subQ0=sQuery(id+"F8.wireOp",EDGE,"E20.MirrorCS");var subQ1=sQuery(id+"F8.wireOp",EDGE,"E19.MirrorCS");Q11=makeQuery(id+"F10.boolean.opBoolean","MERGE",EDGE,{"derivedFrom":[makeQuery(id+"F9.boolean.opBoolean","COPY",EDGE,{"derivedFrom":makeQuery(id+"F9.opExtrude","SWEPT_EDGE",EDGE,{"disambiguationData":[OSD([subQ1,subQ0])]})}),makeQuery(id+"F10.opExtrude","SWEPT_EDGE",EDGE,{"disambiguationData":[OSD([subQ1,subQ0])]})]});}
            fillet(context, id + "F12", {"entities" : qUnion([Q0, Q1, Q2, Q3, Q4, Q5, Q6, Q7, Q8, Q9, Q10, Q11]), "radius" : 0.3 * mm, "tangentPropagation" : true, "allowEdgeOverflow" : false});
        }
        {
            var Q0;
            Q0=makeQuery(id+"F7.opPattern","COPY",EDGE,{"derivedFrom":makeQuery(id+"F2.opExtrude","CAP_EDGE",EDGE,{"disambiguationData":[OSD([sQuery(id+"F0.wireOp",EDGE,"E0")])],"isStart":true}),"instanceName":"1"});
            var Q1;
            Q1=makeQuery(id+"F7.opPattern","COPY",EDGE,{"derivedFrom":makeQuery(id+"F2.opExtrude","CAP_EDGE",EDGE,{"disambiguationData":[OSD([sQuery(id+"F0.wireOp",EDGE,"E0")])],"isStart":false}),"instanceName":"1"});
            var Q2;
            Q2=makeQuery(id+"F2.opExtrude","CAP_EDGE",EDGE,{"disambiguationData":[OSD([sQuery(id+"F0.wireOp",EDGE,"E0")])],"isStart":false});
            var Q3;
            Q3=makeQuery(id+"F2.opExtrude","CAP_EDGE",EDGE,{"disambiguationData":[OSD([sQuery(id+"F0.wireOp",EDGE,"E0")])],"isStart":true});
            fillet(context, id + "F13", {"entities" : qUnion([Q0, Q1, Q2, Q3]), "radius" : 0.2 * mm, "tangentPropagation" : true, "allowEdgeOverflow" : false});
        }
    });
